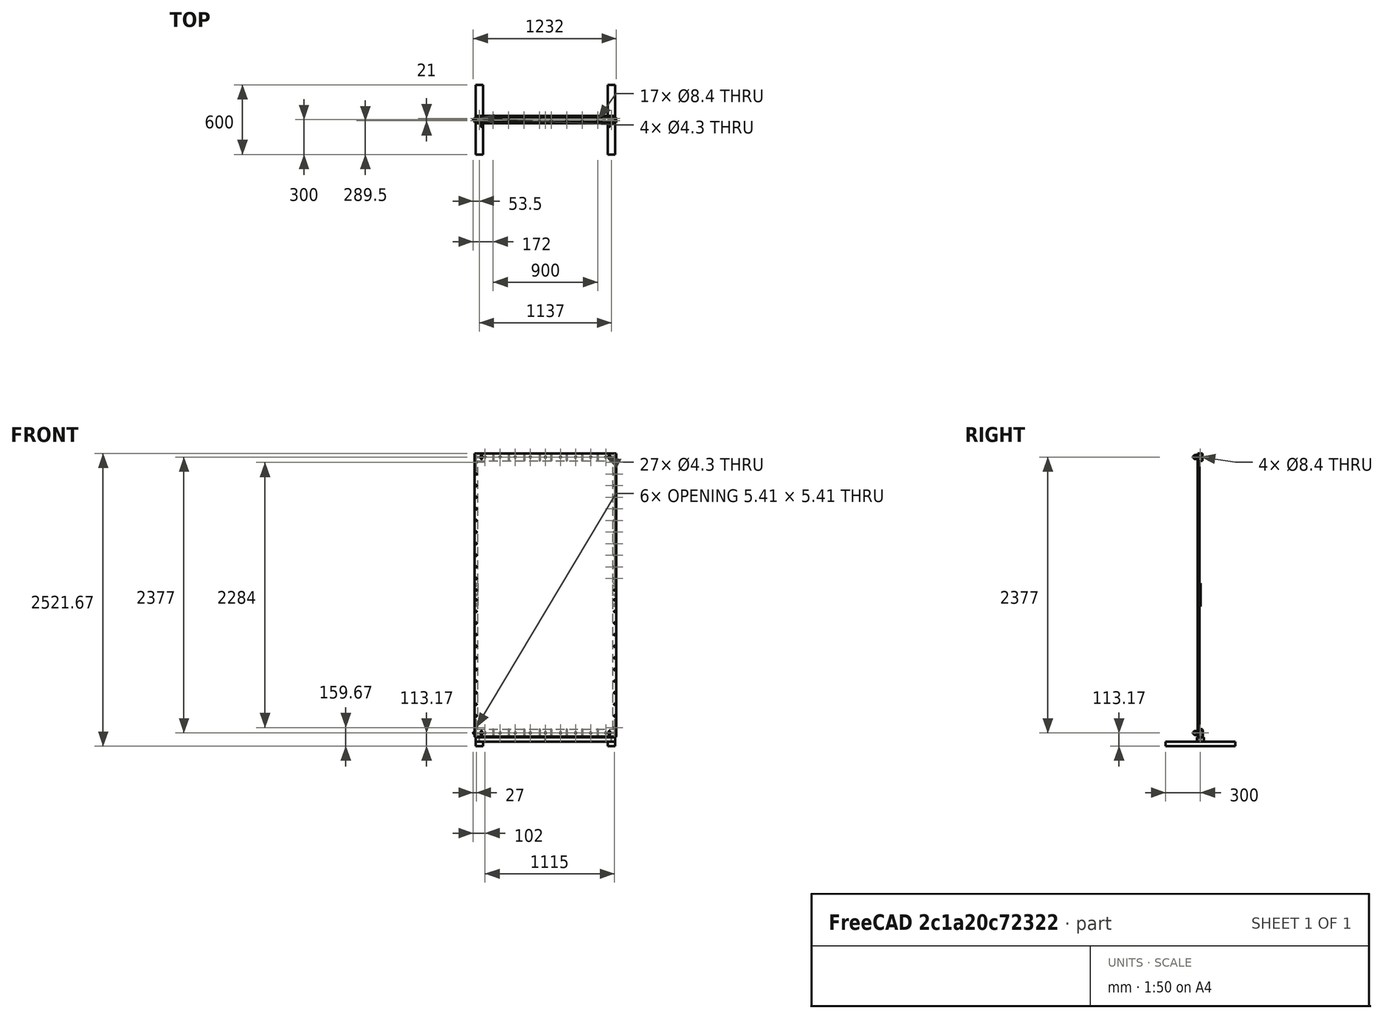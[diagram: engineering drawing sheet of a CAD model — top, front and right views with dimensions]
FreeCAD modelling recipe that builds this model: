
FCSTD DOCUMENT  (FreeCAD 0.21R33771 (Git))
Label: reflector_2024_assembly
License: All rights reserved
LicenseURL: https://en.wikipedia.org/wiki/All_rights_reserved
objects: Part::FeaturePython×30, Part::Compound×4, Part::Feature×4, Part::Mirroring×2, TechDraw::DrawSVGTemplate×1, TechDraw::DrawPage×1
note: 32 computed .brp shape members not serialized (recipe doc carries the construction recipe); baked Part::Feature solids carry a one-line shape summary decoded from their .brp

FEATURE [Part::FeaturePython] b_reflector_2024_panel_001_  label="reflector_2024_panel_panel_001"  # a2plus imported part (geometry in sourceFile) (typed FeaturePython)
  a2p_Version = 0.4.64
  fixedPosition = true
  objectType = a2pPart
  sourceFile = ./reflector_2024_panel.FCStd
  sourcePart = panel
  subassemblyImport = false
  timeLastImport = 1.71015e+09
  updateColors = true
FEATURE [Part::FeaturePython] b_reflector_2024_listello_001_  label="reflector_2024_listello_Body_001"  # a2plus imported part (geometry in sourceFile) (typed FeaturePython)
  Placement = pos=(-595,5,0) rot=(0,0,1;0rad)
  a2p_Version = 0.4.64
  fixedPosition = false
  objectType = a2pPart
  sourceFile = ./reflector_2024_listello.FCStd
  sourcePart = Body
  subassemblyImport = false
  timeLastImport = 1.71015e+09
  updateColors = true
  expr: .Placement.Base.x = -610 + 15
FEATURE [Part::FeaturePython] b_reflector_2024_listello_Body_001_  label="reflector_2024_listello_Body_002"  # a2plus imported part (geometry in sourceFile) (typed FeaturePython)
  Placement = pos=(595,5,0) rot=(0,-1,0;0rad)
  a2p_Version = 0.4.64
  fixedPosition = false
  objectType = a2pPart
  sourceFile = ./reflector_2024_listello.FCStd
  sourcePart = Body
  subassemblyImport = false
  timeLastImport = 1.71015e+09
  updateColors = true
  expr: .Placement.Base.x = 610 - 15
FEATURE [Part::FeaturePython] Screw006  label="M6x12-Screw"  # Fasteners workbench fastener (typed FeaturePython)
  Placement = pos=(595,-6,1142) rot=(1,0,0;1.5708rad)
  diameter = 8
  invert = false
  leftHanded = false
  length = 2
  lengthCustom = 12
  matchOuter = false
  offset = 0
  thread = false
  type = 73
  expr: .Placement.Base.x = 1220 / 2 - 30 / 2
  expr: .Placement.Base.y = -6
  expr: .Placement.Base.z = 1220 - 63 - 15
FEATURE [Part::FeaturePython] Array004  # Draft array (typed FeaturePython)
  AlwaysSyncPlacement = false
  Angle = 360
  ArrayType = 0
  Axis = (0,0,1)
  Base = -> Screw006
  Center = (0,0,0)
  Count = 12
  ExpandArray = false
  Fuse = false
  IntervalAxis = (0,0,0)
  IntervalX = (100,0,0)
  IntervalY = (0,100,0)
  IntervalZ = (0,0,-100)
  NumberCircles = 3
  NumberPolar = 5
  NumberX = 1
  NumberY = 1
  NumberZ = 12
  PlacementList = 12 placements: arithmetic series from (595,-6,1142) step (0,0,-100) to (595,-6,42)
  RadialDistance = 50
  ScaleList = (12) [(1,1,1),(1,1,1),(1,1,1),(1,1,1),(1,1,1),(1,1,1),(1,1,1),(1,1,1),(1,1,1),(1,1,1),(1,1,1),(1,1,1)]
  Symmetry = 1
  TangentialDistance = 25
FEATURE [Part::FeaturePython] Screw007  label="M6x12-Screw001"  # Fasteners workbench fastener (typed FeaturePython)
  Placement = pos=(595,-6,-1142) rot=(1,0,0;1.5708rad)
  diameter = 8
  invert = false
  leftHanded = false
  length = 2
  lengthCustom = 12
  matchOuter = false
  offset = 0
  thread = false
  type = 73
  expr: .Placement.Base.x = 1220 / 2 - 30 / 2
  expr: .Placement.Base.y = -6
  expr: .Placement.Base.z = -(1220 - 63 - 15)
FEATURE [Part::FeaturePython] Array005  # Draft array (typed FeaturePython)
  AlwaysSyncPlacement = false
  Angle = 360
  ArrayType = 0
  Axis = (0,0,1)
  Base = -> Screw007
  Center = (0,0,0)
  Count = 12
  ExpandArray = false
  Fuse = false
  IntervalAxis = (0,0,0)
  IntervalX = (100,0,0)
  IntervalY = (0,100,0)
  IntervalZ = (0,0,100)
  NumberCircles = 3
  NumberPolar = 5
  NumberX = 1
  NumberY = 1
  NumberZ = 12
  PlacementList = 12 placements: arithmetic series from (595,-6,-1142) step (0,0,100) to (595,-6,-42)
  RadialDistance = 50
  ScaleList = (12) [(1,1,1),(1,1,1),(1,1,1),(1,1,1),(1,1,1),(1,1,1),(1,1,1),(1,1,1),(1,1,1),(1,1,1),(1,1,1),(1,1,1)]
  Symmetry = 1
  TangentialDistance = 25
FEATURE [Part::FeaturePython] Screw008  label="M6x12-Screw004"  # Fasteners workbench fastener (typed FeaturePython)
  Placement = pos=(-595,-6,1142) rot=(1,0,0;1.5708rad)
  diameter = 8
  invert = false
  leftHanded = false
  length = 2
  lengthCustom = 12
  matchOuter = false
  offset = 0
  thread = false
  type = 73
  expr: .Placement.Base.x = -(1220 / 2 - 30 / 2)
  expr: .Placement.Base.y = -6
  expr: .Placement.Base.z = 1220 - 63 - 15
FEATURE [Part::FeaturePython] Array006  # Draft array (typed FeaturePython)
  AlwaysSyncPlacement = false
  Angle = 360
  ArrayType = 0
  Axis = (0,0,1)
  Base = -> Screw008
  Center = (0,0,0)
  Count = 12
  ExpandArray = false
  Fuse = false
  IntervalAxis = (0,0,0)
  IntervalX = (100,0,0)
  IntervalY = (0,100,0)
  IntervalZ = (0,0,-100)
  NumberCircles = 3
  NumberPolar = 5
  NumberX = 1
  NumberY = 1
  NumberZ = 12
  PlacementList = 12 placements: arithmetic series from (-595,-6,1142) step (0,0,-100) to (-595,-6,42)
  RadialDistance = 50
  ScaleList = (12) [(1,1,1),(1,1,1),(1,1,1),(1,1,1),(1,1,1),(1,1,1),(1,1,1),(1,1,1),(1,1,1),(1,1,1),(1,1,1),(1,1,1)]
  Symmetry = 1
  TangentialDistance = 25
FEATURE [Part::FeaturePython] Screw009  label="M6x12-Screw005"  # Fasteners workbench fastener (typed FeaturePython)
  Placement = pos=(-595,-6,-1142) rot=(1,0,0;1.5708rad)
  diameter = 8
  invert = false
  leftHanded = false
  length = 2
  lengthCustom = 12
  matchOuter = false
  offset = 0
  thread = false
  type = 73
  expr: .Placement.Base.x = -(1220 / 2 - 30 / 2)
  expr: .Placement.Base.y = -6
  expr: .Placement.Base.z = -(1220 - 63 - 15)
FEATURE [Part::FeaturePython] Array007  # Draft array (typed FeaturePython)
  AlwaysSyncPlacement = false
  Angle = 360
  ArrayType = 0
  Axis = (0,0,1)
  Base = -> Screw009
  Center = (0,0,0)
  Count = 12
  ExpandArray = false
  Fuse = false
  IntervalAxis = (0,0,0)
  IntervalX = (100,0,0)
  IntervalY = (0,100,0)
  IntervalZ = (0,0,100)
  NumberCircles = 3
  NumberPolar = 5
  NumberX = 1
  NumberY = 1
  NumberZ = 12
  PlacementList = 12 placements: arithmetic series from (-595,-6,-1142) step (0,0,100) to (-595,-6,-42)
  RadialDistance = 50
  ScaleList = (12) [(1,1,1),(1,1,1),(1,1,1),(1,1,1),(1,1,1),(1,1,1),(1,1,1),(1,1,1),(1,1,1),(1,1,1),(1,1,1),(1,1,1)]
  Symmetry = 1
  TangentialDistance = 25
FEATURE [Part::FeaturePython] Screw010  label="M6x8-Screw"  # Fasteners workbench fastener (typed FeaturePython)
  Placement = pos=(0,-7,1188.5) rot=(1,0,0;1.5708rad)
  diameter = 8
  invert = false
  leftHanded = false
  length = 0
  lengthCustom = 8
  matchOuter = false
  offset = 0
  thread = false
  type = 73
FEATURE [Part::FeaturePython] Array  # Draft array (typed FeaturePython)
  AlwaysSyncPlacement = false
  Angle = 360
  ArrayType = 0
  Axis = (0,0,1)
  Base = -> Screw010
  Center = (0,0,0)
  Count = 5
  ExpandArray = false
  Fuse = false
  IntervalAxis = (0,0,0)
  IntervalX = (130,0,0)
  IntervalY = (0,100,0)
  IntervalZ = (0,0,100)
  NumberCircles = 3
  NumberPolar = 5
  NumberX = 5
  NumberY = 1
  NumberZ = 1
  PlacementList = 5 placements: arithmetic series from (0,-7,1188.5) step (130,0,0) to (520,-7,1188.5)
  RadialDistance = 50
  ScaleList = (5) [(1,1,1),(1,1,1),(1,1,1),(1,1,1),(1,1,1)]
  Symmetry = 1
  TangentialDistance = 25
FEATURE [Part::Compound] Compound001  label="screws_listelli"
  Links = -> [Array004,Array005,Array006,Array007]
FEATURE [Part::FeaturePython] Array008  # Draft array (typed FeaturePython)
  AlwaysSyncPlacement = false
  Angle = 360
  ArrayType = 0
  Axis = (0,0,1)
  Base = -> Screw010
  Center = (0,0,0)
  Count = 5
  ExpandArray = false
  Fuse = false
  IntervalAxis = (0,0,0)
  IntervalX = (-130,0,0)
  IntervalY = (0,100,0)
  IntervalZ = (0,0,100)
  NumberCircles = 3
  NumberPolar = 5
  NumberX = 5
  NumberY = 1
  NumberZ = 1
  PlacementList = 5 placements: arithmetic series from (0,-7,1188.5) step (-130,0,0) to (-520,-7,1188.5)
  RadialDistance = 50
  ScaleList = (5) [(1,1,1),(1,1,1),(1,1,1),(1,1,1),(1,1,1)]
  Symmetry = 1
  TangentialDistance = 25
FEATURE [Part::FeaturePython] Screw011  label="M6x8-Screw011"  # Fasteners workbench fastener (typed FeaturePython)
  Placement = pos=(0,-7,-1188.5) rot=(1,0,0;1.5708rad)
  diameter = 8
  invert = false
  leftHanded = false
  length = 0
  lengthCustom = 8
  matchOuter = false
  offset = 0
  thread = false
  type = 73
  expr: .Placement.Base.z = -1188.5 mm
FEATURE [Part::FeaturePython] Array009  # Draft array (typed FeaturePython)
  AlwaysSyncPlacement = false
  Angle = 360
  ArrayType = 0
  Axis = (0,0,1)
  Base = -> Screw011
  Center = (0,0,0)
  Count = 5
  ExpandArray = false
  Fuse = false
  IntervalAxis = (0,0,0)
  IntervalX = (130,0,0)
  IntervalY = (0,100,0)
  IntervalZ = (0,0,100)
  NumberCircles = 3
  NumberPolar = 5
  NumberX = 5
  NumberY = 1
  NumberZ = 1
  PlacementList = 5 placements: arithmetic series from (0,-7,-1188.5) step (130,0,0) to (520,-7,-1188.5)
  RadialDistance = 50
  ScaleList = (5) [(1,1,1),(1,1,1),(1,1,1),(1,1,1),(1,1,1)]
  Symmetry = 1
  TangentialDistance = 25
FEATURE [Part::FeaturePython] Array010  # Draft array (typed FeaturePython)
  AlwaysSyncPlacement = false
  Angle = 360
  ArrayType = 0
  Axis = (0,0,1)
  Base = -> Screw011
  Center = (0,0,0)
  Count = 5
  ExpandArray = false
  Fuse = false
  IntervalAxis = (0,0,0)
  IntervalX = (-130,0,0)
  IntervalY = (0,100,0)
  IntervalZ = (0,0,100)
  NumberCircles = 3
  NumberPolar = 5
  NumberX = 5
  NumberY = 1
  NumberZ = 1
  PlacementList = 5 placements: arithmetic series from (0,-7,-1188.5) step (-130,0,0) to (-520,-7,-1188.5)
  RadialDistance = 50
  ScaleList = (5) [(1,1,1),(1,1,1),(1,1,1),(1,1,1),(1,1,1)]
  Symmetry = 1
  TangentialDistance = 25
FEATURE [Part::Compound] Compound  label="screws_battens"
  Links = -> [Array,Array008,Array009,Array010]
FEATURE [Part::Feature] Part__Feature  label="LIFTING EYE BOLT - M8 - DIN 580_1"
  Placement = pos=(550,-25,1188.5) rot=(0.707107,0,-0.707107;3.14159rad)
  shape: bbox 21.03 x 49.35 x 36.93 mm, 59 faces (baked)
  expr: .Placement.Base.x = 610 - 60
  expr: .Placement.Base.z = 1220 - 63 / 2
FEATURE [Part::Feature] Part__Feature001  label="LIFTING EYE BOLT - M8 - DIN 580_2"
  Placement = pos=(-550,-25,1188.5) rot=(0.707107,0,-0.707107;3.14159rad)
  shape: bbox 21.03 x 49.35 x 36.93 mm, 59 faces (baked)
  expr: .Placement.Base.x = -(610 - 60)
  expr: .Placement.Base.z = 1220 - 63 / 2
FEATURE [Part::Feature] Part__Feature002  label="LIFTING EYE BOLT - M8 - DIN 580_3"
  Placement = pos=(550,-25,-1188.5) rot=(0.707107,0,-0.707107;3.14159rad)
  shape: bbox 21.03 x 49.35 x 36.93 mm, 59 faces (baked)
  expr: .Placement.Base.x = 610 - 60
  expr: .Placement.Base.z = -(1220 - 63 / 2)
FEATURE [Part::Feature] Part__Feature003  label="LIFTING EYE BOLT - M8 - DIN 580_4"
  Placement = pos=(-550,-25,-1188.5) rot=(0.707107,0,-0.707107;3.14159rad)
  shape: bbox 21.03 x 49.35 x 36.93 mm, 59 faces (baked)
  expr: .Placement.Base.x = -(610 - 60)
  expr: .Placement.Base.z = -(1220 - 63 / 2)
FEATURE [Part::Compound] Compound002  label="eye_bolts"
  Links = -> [Part__Feature,Part__Feature001,Part__Feature002,Part__Feature003]
FEATURE [Part::FeaturePython] b_reflector_2024_listello_handle_001_  label="reflector_2024_listello_handle_001"  # a2plus imported part (geometry in sourceFile) (typed FeaturePython)
  Placement = pos=(595,20,0) rot=(0,0,1;0rad)
  a2p_Version = 0.4.64
  fixedPosition = false
  objectType = a2pPart
  sourceFile = ./reflector_2024_listello_handle.FCStd
  subassemblyImport = false
  timeLastImport = 1709987877
  updateColors = true
  expr: .Placement.Base.x = 610 - 15
FEATURE [Part::FeaturePython] b_reflector_2024_listello_handle_001_001  label="reflector_2024_listello_handle_002"  # a2plus imported part (geometry in sourceFile) (typed FeaturePython)
  Placement = pos=(-595,20,0) rot=(0,0,1;0rad)
  a2p_Version = 0.4.64
  fixedPosition = false
  objectType = a2pPart
  sourceFile = ./reflector_2024_listello_handle.FCStd
  subassemblyImport = false
  timeLastImport = 1709987877
  updateColors = true
  expr: .Placement.Base.x = -610 + 15
FEATURE [Part::FeaturePython] Screw  label="M6x25-Screw"  # Fasteners workbench fastener (typed FeaturePython)
  Placement = pos=(595,21,0) rot=(-1,0,0;1.5708rad)
  diameter = 8
  invert = false
  leftHanded = false
  length = 6
  lengthCustom = 25
  matchOuter = false
  offset = 0
  thread = false
  type = 73
  expr: .Placement.Base.x = 610 - 15
FEATURE [Part::FeaturePython] Screw012  label="M6x25-Screw001"  # Fasteners workbench fastener (typed FeaturePython)
  Placement = pos=(595,21,80) rot=(-1,0,0;1.5708rad)
  diameter = 8
  invert = false
  leftHanded = false
  length = 6
  lengthCustom = 25
  matchOuter = false
  offset = 0
  thread = false
  type = 73
  expr: .Placement.Base.x = 610 - 15
FEATURE [Part::FeaturePython] Screw013  label="M6x25-Screw002"  # Fasteners workbench fastener (typed FeaturePython)
  Placement = pos=(595,21,-80) rot=(-1,0,0;1.5708rad)
  diameter = 8
  invert = false
  leftHanded = false
  length = 6
  lengthCustom = 25
  matchOuter = false
  offset = 0
  thread = false
  type = 73
  expr: .Placement.Base.x = 610 - 15
FEATURE [Part::FeaturePython] Screw014  label="M6x25-Screw003"  # Fasteners workbench fastener (typed FeaturePython)
  Placement = pos=(-595,21,0) rot=(-1,0,0;1.5708rad)
  diameter = 8
  invert = false
  leftHanded = false
  length = 6
  lengthCustom = 25
  matchOuter = false
  offset = 0
  thread = false
  type = 73
  expr: .Placement.Base.x = -610 + 15
FEATURE [Part::FeaturePython] Screw015  label="M6x25-Screw004"  # Fasteners workbench fastener (typed FeaturePython)
  Placement = pos=(-595,21,80) rot=(-1,0,0;1.5708rad)
  diameter = 8
  invert = false
  leftHanded = false
  length = 6
  lengthCustom = 25
  matchOuter = false
  offset = 0
  thread = false
  type = 73
  expr: .Placement.Base.x = -610 + 15
FEATURE [Part::FeaturePython] Screw016  label="M6x25-Screw005"  # Fasteners workbench fastener (typed FeaturePython)
  Placement = pos=(-595,21,-80) rot=(-1,0,0;1.5708rad)
  diameter = 8
  invert = false
  leftHanded = false
  length = 6
  lengthCustom = 25
  matchOuter = false
  offset = 0
  thread = false
  type = 73
  expr: .Placement.Base.x = -610 + 15
FEATURE [Part::Compound] Compound003  label="screws_handles"
  Links = -> [Screw,Screw012,Screw013,Screw014,Screw015,Screw016]
FEATURE [Part::FeaturePython] b_reflector_2024_timber_001_  label="reflector_2024_timber_001"  # a2plus imported part (geometry in sourceFile) (typed FeaturePython)
  Placement = pos=(0,19,1188.5) rot=(0,0,1;0rad)
  a2p_Version = 0.4.64
  fixedPosition = false
  objectType = a2pPart
  sourceFile = ./reflector_2024_timber.FCStd
  subassemblyImport = false
  timeLastImport = 1.71015e+09
  updateColors = true
  expr: .Placement.Base.y = 38 / 2
FEATURE [Part::FeaturePython] b_reflector_2024_timber_001_001  label="reflector_2024_timber_002"  # a2plus imported part (geometry in sourceFile) (typed FeaturePython)
  Placement = pos=(0,19,-1188.5) rot=(0,0,1;0rad)
  a2p_Version = 0.4.64
  fixedPosition = false
  objectType = a2pPart
  sourceFile = ./reflector_2024_timber.FCStd
  subassemblyImport = false
  timeLastImport = 1.71015e+09
  updateColors = true
  expr: .Placement.Base.y = 38 / 2
FEATURE [TechDraw::DrawSVGTemplate] Template
  Height = 594
  Orientation = 1
  Template = /snap/freecad/908/usr/share/Mod/TechDraw/Templates/A1_Landscape_blank.svg
  Width = 841
FEATURE [TechDraw::DrawPage] Page
  KeepUpdated = true
  NextBalloonIndex = 1
  ProjectionType = 0
  Template = -> Template
FEATURE [Part::FeaturePython] ScrewTap  label="M8x35-ScrewTap"  # Fasteners workbench fastener (typed FeaturePython)
  Placement = pos=(622,19,-1188.5) rot=(0,1,0;1.5708rad)
  diameter = 9
  diameterCustom = 6
  invert = false
  leftHanded = false
  length = 35
  matchOuter = false
  offset = 0
  pitchCustom = 1
  thread = false
  type = 2
  expr: .Placement.Base.y = 38 / 2
  expr: .Placement.Base.z = -1220 + 63 / 2
FEATURE [Part::Mirroring] Mirror  label="M8x35-ScrewTap (mirrored)"
  Base = (0,0,0)
  Normal = (1,0,0)
  Source = -> ScrewTap
FEATURE [Part::FeaturePython] b_reflector_2024_base_001_  label="reflector_2024_base_001"  # a2plus imported part (geometry in sourceFile) (typed FeaturePython)
  Placement = pos=(0,19,-1244.67) rot=(0,0,1;0rad)
  a2p_Version = 0.4.64
  fixedPosition = false
  objectType = a2pPart
  sourceFile = .\reflector_2024_base.FCStd
  subassemblyImport = true
  timeLastImport = 1.71052e+09
  updateColors = true
FEATURE [Part::FeaturePython] Nut  label="M8-Nut"  # Fasteners workbench fastener (typed FeaturePython)
  Placement = pos=(612,19,-1188.5) rot=(0,1,0;1.5708rad)
  diameter = 3
  invert = false
  leftHanded = false
  matchOuter = false
  offset = 0
  thread = false
  type = 32
  expr: .Placement.Base.y = 38 / 2
  expr: .Placement.Base.z = -1220 + 63 / 2
FEATURE [Part::Mirroring] Mirror001  label="M8-Nut (mirrored)"
  Base = (0,0,0)
  Normal = (1,0,0)
  Source = -> Nut
